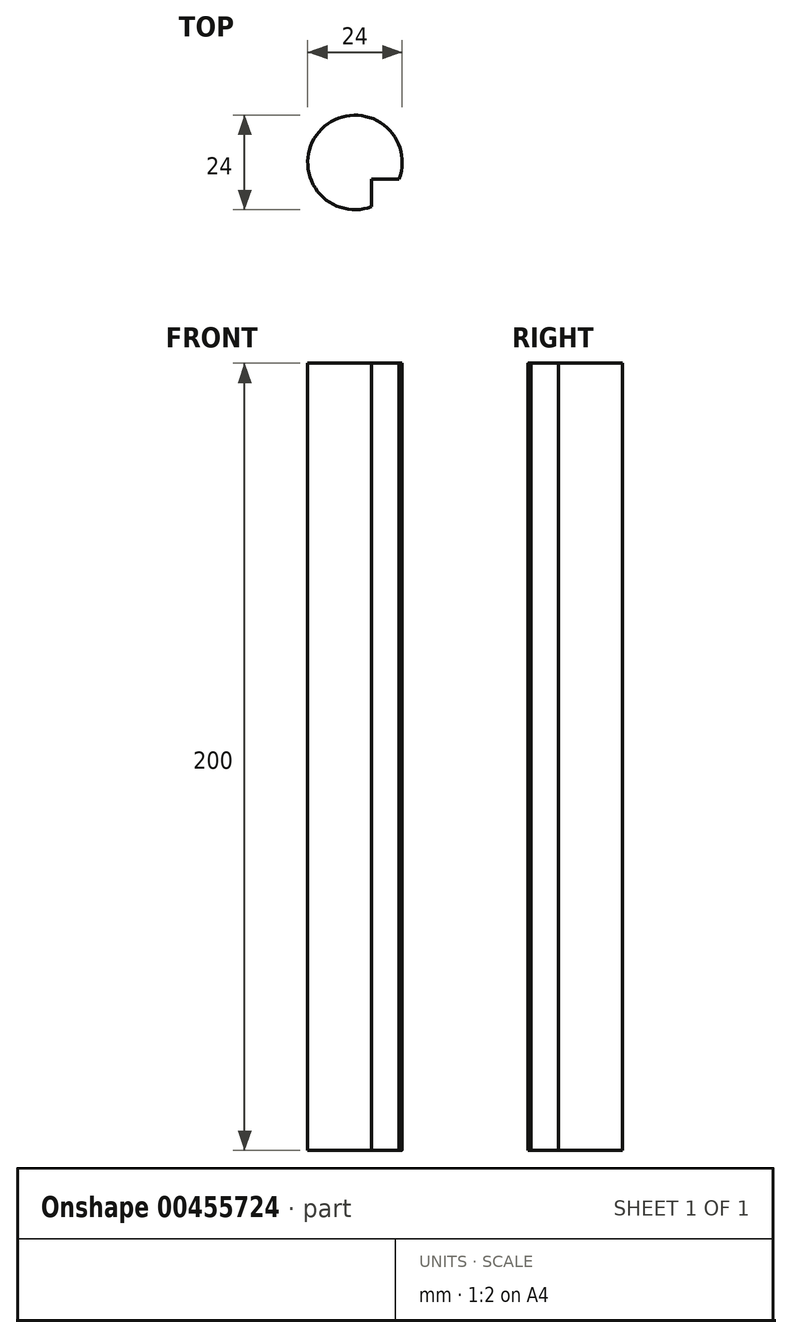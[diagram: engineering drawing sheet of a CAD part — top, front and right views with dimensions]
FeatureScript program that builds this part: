
annotation { "Feature Type Name" : "Feature", "Feature Type Description" : "" }
export const myFeature = defineFeature(function(context is Context, id is Id, definition is map)
    precondition{}
    {
        {
            var Q0;
            Q0=qCreatedBy(makeId("Top.planeOp"),FACE);
            var sketch = newSketch(context, id + "F0", { "sketchPlane" : qUnion([Q0])});
            skCircle(sketch, "E0", {"center": v(0, 0) * mm, "radius": 12 * mm});
            skSolve(sketch);
        }
        {
            var Q0;
            Q0 = qSketchRegion(id + "F0", true);
            extrude(context, id + "F1", {"entities" : qUnion([Q0]), "depth" : 200 * mm});
        }
        {
            var Q0;
            Q0=makeQuery(id+"F1.opExtrude","CAP_FACE",FACE,{"disambiguationData":[OSD([sQuery(id+"F0.wireOp",EDGE,"E0")])],"isStart":false});
            var sketch = newSketch(context, id + "F2", { "sketchPlane" : qUnion([Q0])});
            skLineSegment(sketch, "E1", {"start": v(0, 0) * mm, "end": v(8.49, -8.49) * mm, "construction": true});
            skLineSegment(sketch, "E2", {"start": v(4.24, -4.24) * mm, "end": v(4.24, -11.22) * mm});
            skLineSegment(sketch, "E3", {"start": v(4.24, -4.24) * mm, "end": v(11.22, -4.24) * mm});
            skSolve(sketch);
        }
        {
            var Q0;
            {var subQ0=sQuery(id+"F2.wireOp",EDGE,"E2");Q0=makeQuery(id+"F2.imprint","IMPRINT",FACE,{"disambiguationData":[TD([[makeQuery(id+"F2.imprint","IMPRINT",EDGE,{"derivedFrom":subQ0}),1.0]])]});}
            extrude(context, id + "F3", {"entities" : qUnion([Q0]), "operationType" : NewBodyOperationType.REMOVE, "endBound" : BoundingType.THROUGH_ALL, "oppositeDirection" : true, "depth" : 25 * mm});
        }
    });
